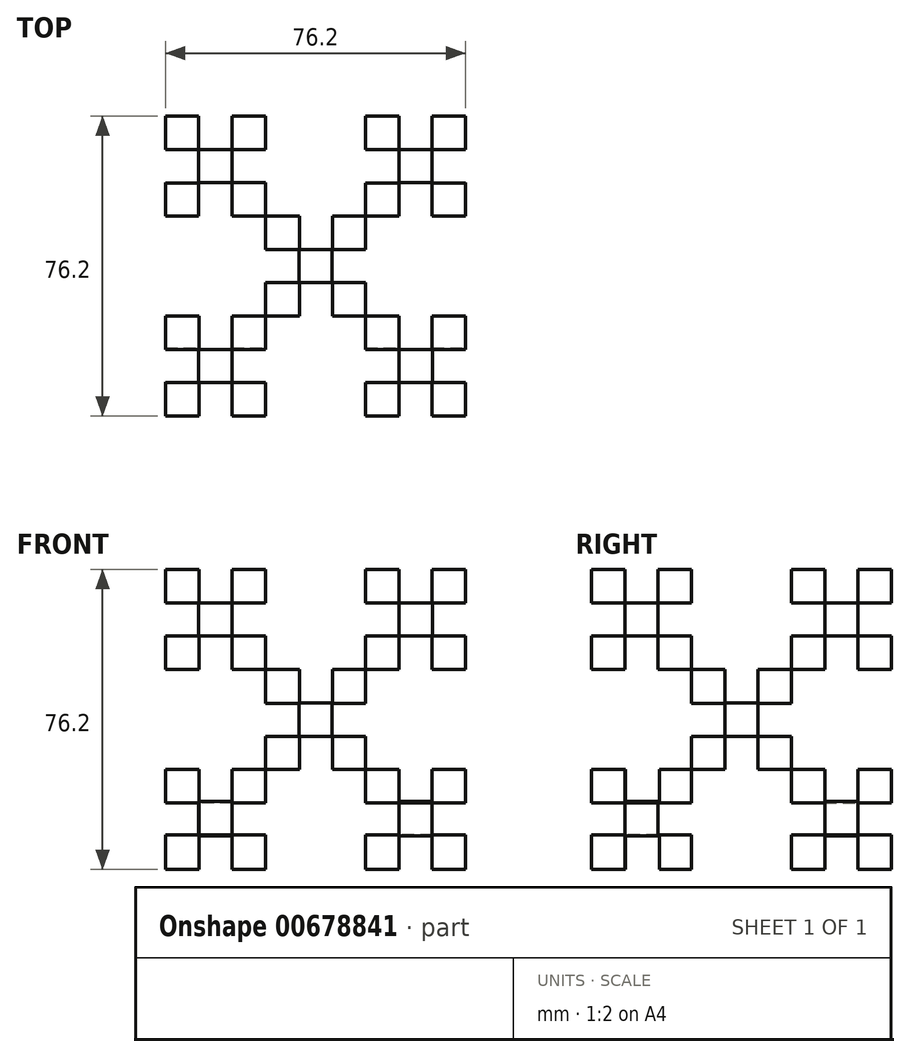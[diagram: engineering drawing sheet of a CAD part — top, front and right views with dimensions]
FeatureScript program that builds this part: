
annotation { "Feature Type Name" : "Feature", "Feature Type Description" : "" }
export const myFeature = defineFeature(function(context is Context, id is Id, definition is map)
    precondition{}
    {
        {
            var Q0;
            Q0=qCreatedBy(makeId("Front.planeOp"),FACE);
            var sketch = newSketch(context, id + "F0", { "sketchPlane" : qUnion([Q0])});
            skLineSegment(sketch, "E0.bottom", {"start": v(-38.1, 38.1) * mm, "end": v(38.1, 38.1) * mm});
            skLineSegment(sketch, "E0.top", {"start": v(-38.1, -38.1) * mm, "end": v(38.1, -38.1) * mm});
            skLineSegment(sketch, "E0.left", {"start": v(-38.1, 38.1) * mm, "end": v(-38.1, -38.1) * mm});
            skLineSegment(sketch, "E0.right", {"start": v(38.1, 38.1) * mm, "end": v(38.1, -38.1) * mm});
            skPoint(sketch, "E0.middle", {"position": v(0, 0) * mm});
            skSolve(sketch);
        }
        {
            var Q0;
            Q0=makeQuery(id+"F0.imprint","IMPRINT",FACE,{"disambiguationData":[TD([[makeQuery(id+"F0.imprint","IMPRINT",EDGE,{"derivedFrom":sQuery(id+"F0.wireOp",EDGE,"E0.bottom")}),-1.0]])]});
            extrude(context, id + "F1", {"entities" : qUnion([Q0]), "depth" : 76.2 * mm, "offsetDistance" : 25.4 * mm});
        }
        {
            var Q0;
            Q0=qCreatedBy(makeId("Front.planeOp"),FACE);
            var sketch = newSketch(context, id + "F2", { "sketchPlane" : qUnion([Q0])});
            skLineSegment(sketch, "E1.bottom", {"start": v(12.7, 12.7) * mm, "end": v(-12.7, 12.7) * mm});
            skLineSegment(sketch, "E1.top", {"start": v(12.7, -12.7) * mm, "end": v(-12.7, -12.7) * mm});
            skLineSegment(sketch, "E1.left", {"start": v(12.7, 12.7) * mm, "end": v(12.7, -12.7) * mm});
            skLineSegment(sketch, "E1.right", {"start": v(-12.7, 12.7) * mm, "end": v(-12.7, -12.7) * mm});
            skPoint(sketch, "E1.middle", {"position": v(0, 0) * mm});
            skLineSegment(sketch, "E2.top", {"start": v(12.7, 38.1) * mm, "end": v(-12.7, 38.1) * mm});
            skLineSegment(sketch, "E2.left", {"start": v(12.7, 12.7) * mm, "end": v(12.7, 38.1) * mm});
            skLineSegment(sketch, "E2.right", {"start": v(-12.7, 12.7) * mm, "end": v(-12.7, 38.1) * mm});
            skLineSegment(sketch, "E3.bottom", {"start": v(-12.7, 12.7) * mm, "end": v(-38.1, 12.7) * mm});
            skLineSegment(sketch, "E3.top", {"start": v(-12.7, -12.7) * mm, "end": v(-38.1, -12.7) * mm});
            skLineSegment(sketch, "E3.right", {"start": v(-38.1, 12.7) * mm, "end": v(-38.1, -12.7) * mm});
            skLineSegment(sketch, "E4.top", {"start": v(12.7, -38.1) * mm, "end": v(-12.7, -38.1) * mm});
            skLineSegment(sketch, "E4.left", {"start": v(12.7, -12.7) * mm, "end": v(12.7, -38.1) * mm});
            skLineSegment(sketch, "E4.right", {"start": v(-12.7, -12.7) * mm, "end": v(-12.7, -38.1) * mm});
            skLineSegment(sketch, "E5.bottom", {"start": v(12.7, 12.7) * mm, "end": v(38.1, 12.7) * mm});
            skLineSegment(sketch, "E5.top", {"start": v(12.7, -12.7) * mm, "end": v(38.1, -12.7) * mm});
            skLineSegment(sketch, "E5.right", {"start": v(38.1, 12.7) * mm, "end": v(38.1, -12.7) * mm});
            skSolve(sketch);
        }
        {
            var Q0;
            Q0 = qSketchRegion(id + "F2", true);
            extrude(context, id + "F3", {"entities" : qUnion([Q0]), "operationType" : NewBodyOperationType.REMOVE, "depth" : 25.4 * mm, "offsetDistance" : 25.4 * mm});
        }
        {
            var Q0;
            Q0=qCreatedBy(makeId("Front.planeOp"),FACE);
            cPlane(context, id + "F4", {"entities" : qUnion([Q0]), "cplaneType" : CPlaneType.OFFSET, "offset" : 76.2 * mm, "width" : 152.4 * mm, "height" : 152.4 * mm});
        }
        {
            var Q0;
            Q0=qCreatedBy(id+"F4.planeOp",FACE);
            var sketch = newSketch(context, id + "F5", { "sketchPlane" : qUnion([Q0])});
            skLineSegment(sketch, "E6.bottom", {"start": v(-12.7, 12.7) * mm, "end": v(12.7, 12.7) * mm});
            skLineSegment(sketch, "E6.top", {"start": v(-12.7, -12.7) * mm, "end": v(12.7, -12.7) * mm});
            skLineSegment(sketch, "E6.left", {"start": v(-12.7, 12.7) * mm, "end": v(-12.7, -12.7) * mm});
            skLineSegment(sketch, "E6.right", {"start": v(12.7, 12.7) * mm, "end": v(12.7, -12.7) * mm});
            skPoint(sketch, "E6.middle", {"position": v(0, 0) * mm});
            skLineSegment(sketch, "E7.top", {"start": v(-12.7, 38.1) * mm, "end": v(12.7, 38.1) * mm});
            skLineSegment(sketch, "E7.left", {"start": v(-12.7, 12.7) * mm, "end": v(-12.7, 38.1) * mm});
            skLineSegment(sketch, "E7.right", {"start": v(12.7, 12.7) * mm, "end": v(12.7, 38.1) * mm});
            skLineSegment(sketch, "E8.left", {"start": v(-12.7, -12.7) * mm, "end": v(-12.7, -12.7) * mm});
            skLineSegment(sketch, "E8.right", {"start": v(12.7, -12.7) * mm, "end": v(12.7, -12.7) * mm});
            skLineSegment(sketch, "E9.top", {"start": v(-12.7, -38.1) * mm, "end": v(12.7, -38.1) * mm});
            skLineSegment(sketch, "E9.left", {"start": v(-12.7, -12.7) * mm, "end": v(-12.7, -38.1) * mm});
            skLineSegment(sketch, "E9.right", {"start": v(12.7, -12.7) * mm, "end": v(12.7, -38.1) * mm});
            skLineSegment(sketch, "E10.bottom", {"start": v(12.7, 12.7) * mm, "end": v(38.1, 12.7) * mm});
            skLineSegment(sketch, "E10.top", {"start": v(12.7, -12.7) * mm, "end": v(38.1, -12.7) * mm});
            skLineSegment(sketch, "E10.right", {"start": v(38.1, 12.7) * mm, "end": v(38.1, -12.7) * mm});
            skLineSegment(sketch, "E11.bottom", {"start": v(-12.7, -12.7) * mm, "end": v(-38.1, -12.7) * mm});
            skLineSegment(sketch, "E11.top", {"start": v(-12.7, 12.7) * mm, "end": v(-38.1, 12.7) * mm});
            skLineSegment(sketch, "E11.left", {"start": v(-12.7, -12.7) * mm, "end": v(-12.7, 12.7) * mm});
            skLineSegment(sketch, "E11.right", {"start": v(-38.1, -12.7) * mm, "end": v(-38.1, 12.7) * mm});
            skSolve(sketch);
        }
        {
            var Q0;
            Q0 = qSketchRegion(id + "F5", true);
            extrude(context, id + "F6", {"entities" : qUnion([Q0]), "operationType" : NewBodyOperationType.REMOVE, "oppositeDirection" : true, "depth" : 25.4 * mm, "offsetDistance" : 25.4 * mm});
        }
        {
            var Q0;
            Q0=qCreatedBy(makeId("Top.planeOp"),FACE);
            cPlane(context, id + "F7", {"entities" : qUnion([Q0]), "cplaneType" : CPlaneType.OFFSET, "offset" : 38.1 * mm, "width" : 152.4 * mm, "height" : 152.4 * mm});
        }
        {
            var Q0;
            Q0=qCreatedBy(id+"F7.planeOp",FACE);
            var sketch = newSketch(context, id + "F8", { "sketchPlane" : qUnion([Q0])});
            skLineSegment(sketch, "E12.bottom", {"start": v(-12.7, -25.4) * mm, "end": v(12.7, -25.4) * mm});
            skLineSegment(sketch, "E12.top", {"start": v(-12.7, -50.8) * mm, "end": v(12.7, -50.8) * mm});
            skLineSegment(sketch, "E12.left", {"start": v(-12.7, -25.4) * mm, "end": v(-12.7, -50.8) * mm});
            skLineSegment(sketch, "E12.right", {"start": v(12.7, -25.4) * mm, "end": v(12.7, -50.8) * mm});
            skPoint(sketch, "E12.middle", {"position": v(0, -38.1) * mm});
            skLineSegment(sketch, "E13.bottom", {"start": v(12.7, -25.4) * mm, "end": v(38.1, -25.4) * mm});
            skLineSegment(sketch, "E13.top", {"start": v(12.7, -50.8) * mm, "end": v(38.1, -50.8) * mm});
            skLineSegment(sketch, "E13.right", {"start": v(38.1, -25.4) * mm, "end": v(38.1, -50.8) * mm});
            skLineSegment(sketch, "E14.bottom", {"start": v(-12.7, -25.4) * mm, "end": v(-38.1, -25.4) * mm});
            skLineSegment(sketch, "E14.top", {"start": v(-12.7, -50.8) * mm, "end": v(-38.1, -50.8) * mm});
            skLineSegment(sketch, "E14.right", {"start": v(-38.1, -25.4) * mm, "end": v(-38.1, -50.8) * mm});
            skSolve(sketch);
        }
        {
            var Q0;
            Q0 = qSketchRegion(id + "F8", true);
            extrude(context, id + "F9", {"entities" : qUnion([Q0]), "operationType" : NewBodyOperationType.REMOVE, "oppositeDirection" : true, "depth" : 25.4 * mm, "offsetDistance" : 25.4 * mm});
        }
        {
            var Q0;
            Q0=qCreatedBy(makeId("Right.planeOp"),FACE);
            cPlane(context, id + "F10", {"entities" : qUnion([Q0]), "cplaneType" : CPlaneType.OFFSET, "offset" : 38.1 * mm, "width" : 152.4 * mm, "height" : 152.4 * mm});
        }
        {
            var Q0;
            Q0=qCreatedBy(id+"F10.planeOp",FACE);
            var sketch = newSketch(context, id + "F11", { "sketchPlane" : qUnion([Q0])});
            skLineSegment(sketch, "E15", {"start": v(0, 0) * mm, "end": v(-38.1, 0) * mm});
            skLineSegment(sketch, "E16.bottom", {"start": v(-50.8, 12.7) * mm, "end": v(-25.4, 12.7) * mm});
            skLineSegment(sketch, "E16.top", {"start": v(-50.8, -12.7) * mm, "end": v(-25.4, -12.7) * mm});
            skLineSegment(sketch, "E16.left", {"start": v(-50.8, 12.7) * mm, "end": v(-50.8, -12.7) * mm});
            skLineSegment(sketch, "E16.right", {"start": v(-25.4, 12.7) * mm, "end": v(-25.4, -12.7) * mm});
            skPoint(sketch, "E16.middle", {"position": v(-38.1, 0) * mm});
            skLineSegment(sketch, "E17.bottom", {"start": v(-25.4, -12.7) * mm, "end": v(-50.8, -12.7) * mm});
            skLineSegment(sketch, "E17.top", {"start": v(-25.4, -38.1) * mm, "end": v(-50.8, -38.1) * mm});
            skLineSegment(sketch, "E17.left", {"start": v(-25.4, -12.7) * mm, "end": v(-25.4, -38.1) * mm});
            skLineSegment(sketch, "E17.right", {"start": v(-50.8, -12.7) * mm, "end": v(-50.8, -38.1) * mm});
            skSolve(sketch);
        }
        {
            var Q0;
            Q0 = qSketchRegion(id + "F11", true);
            extrude(context, id + "F12", {"entities" : qUnion([Q0]), "operationType" : NewBodyOperationType.REMOVE, "oppositeDirection" : true, "depth" : 25.4 * mm, "offsetDistance" : 25.4 * mm});
        }
        {
            var Q0;
            Q0=qCreatedBy(makeId("Top.planeOp"),FACE);
            cPlane(context, id + "F13", {"entities" : qUnion([Q0]), "cplaneType" : CPlaneType.OFFSET, "offset" : 38.1 * mm, "oppositeDirection" : true, "width" : 152.4 * mm, "height" : 152.4 * mm});
        }
        {
            var Q0;
            Q0=qCreatedBy(id+"F13.planeOp",FACE);
            var sketch = newSketch(context, id + "F14", { "sketchPlane" : qUnion([Q0])});
            skLineSegment(sketch, "E18", {"start": v(0, 0) * mm, "end": v(0, -38.1) * mm});
            skLineSegment(sketch, "E19.bottom", {"start": v(-12.7, -50.8) * mm, "end": v(12.7, -50.8) * mm});
            skLineSegment(sketch, "E19.top", {"start": v(-12.7, -25.4) * mm, "end": v(12.7, -25.4) * mm});
            skLineSegment(sketch, "E19.left", {"start": v(-12.7, -50.8) * mm, "end": v(-12.7, -25.4) * mm});
            skLineSegment(sketch, "E19.right", {"start": v(12.7, -50.8) * mm, "end": v(12.7, -25.4) * mm});
            skPoint(sketch, "E19.middle", {"position": v(0, -38.1) * mm});
            skLineSegment(sketch, "E20.bottom", {"start": v(-12.7, -50.8) * mm, "end": v(-38.1, -50.8) * mm});
            skLineSegment(sketch, "E20.top", {"start": v(-12.7, -25.4) * mm, "end": v(-38.1, -25.4) * mm});
            skLineSegment(sketch, "E20.right", {"start": v(-38.1, -50.8) * mm, "end": v(-38.1, -25.4) * mm});
            skSolve(sketch);
        }
        {
            var Q0;
            Q0 = qSketchRegion(id + "F14", true);
            extrude(context, id + "F15", {"entities" : qUnion([Q0]), "operationType" : NewBodyOperationType.REMOVE, "depth" : 25.4 * mm, "offsetDistance" : 25.4 * mm});
        }
        {
            var Q0;
            Q0=qCreatedBy(makeId("Right.planeOp"),FACE);
            cPlane(context, id + "F16", {"entities" : qUnion([Q0]), "cplaneType" : CPlaneType.OFFSET, "offset" : 38.1 * mm, "oppositeDirection" : true, "width" : 152.4 * mm, "height" : 152.4 * mm});
        }
        {
            var Q0;
            Q0=qCreatedBy(id+"F16.planeOp",FACE);
            var sketch = newSketch(context, id + "F17", { "sketchPlane" : qUnion([Q0])});
            skLineSegment(sketch, "E21.bottom", {"start": v(-25.4, 12.7) * mm, "end": v(-50.8, 12.7) * mm});
            skLineSegment(sketch, "E21.top", {"start": v(-25.4, -12.7) * mm, "end": v(-50.8, -12.7) * mm});
            skLineSegment(sketch, "E21.left", {"start": v(-25.4, 12.7) * mm, "end": v(-25.4, -12.7) * mm});
            skLineSegment(sketch, "E21.right", {"start": v(-50.8, 12.7) * mm, "end": v(-50.8, -12.7) * mm});
            skPoint(sketch, "E21.middle", {"position": v(-38.1, 0) * mm});
            skSolve(sketch);
        }
        {
            var Q0;
            Q0 = qSketchRegion(id + "F17", true);
            extrude(context, id + "F18", {"entities" : qUnion([Q0]), "operationType" : NewBodyOperationType.REMOVE, "depth" : 25.4 * mm, "offsetDistance" : 25.4 * mm});
        }
        {
            var Q0;
            Q0=qCreatedBy(id+"F10.planeOp",FACE);
            var sketch = newSketch(context, id + "F19", { "sketchPlane" : qUnion([Q0])});
            skLineSegment(sketch, "E22.bottom", {"start": v(-8.48, 29.64) * mm, "end": v(-16.95, 29.64) * mm});
            skLineSegment(sketch, "E22.top", {"start": v(-8.48, 21.18) * mm, "end": v(-16.95, 21.18) * mm});
            skLineSegment(sketch, "E22.left", {"start": v(-8.48, 29.64) * mm, "end": v(-8.48, 21.18) * mm});
            skLineSegment(sketch, "E22.right", {"start": v(-16.95, 29.64) * mm, "end": v(-16.95, 21.18) * mm});
            skPoint(sketch, "E22.middle", {"position": v(-12.72, 25.41) * mm});
            skLineSegment(sketch, "E23.top", {"start": v(-8.48, 38.1) * mm, "end": v(-16.95, 38.1) * mm});
            skLineSegment(sketch, "E23.left", {"start": v(-8.48, 29.64) * mm, "end": v(-8.48, 38.1) * mm});
            skLineSegment(sketch, "E23.right", {"start": v(-16.95, 29.64) * mm, "end": v(-16.95, 38.1) * mm});
            skLineSegment(sketch, "E24.top", {"start": v(-8.48, 12.7) * mm, "end": v(-16.95, 12.7) * mm});
            skLineSegment(sketch, "E24.left", {"start": v(-8.48, 38.1) * mm, "end": v(-8.48, 12.7) * mm});
            skLineSegment(sketch, "E24.right", {"start": v(-16.95, 38.1) * mm, "end": v(-16.95, 12.7) * mm});
            skLineSegment(sketch, "E25.bottom", {"start": v(0, 21.19) * mm, "end": v(0, 29.64) * mm});
            skLineSegment(sketch, "E25.top", {"start": v(-25.4, 21.19) * mm, "end": v(-25.4, 29.64) * mm});
            skLineSegment(sketch, "E25.left", {"start": v(0, 21.19) * mm, "end": v(-25.4, 21.19) * mm});
            skLineSegment(sketch, "E25.right", {"start": v(0, 29.64) * mm, "end": v(-25.4, 29.64) * mm});
            skLineSegment(sketch, "E26.bottom", {"start": v(-8.48, -21.17) * mm, "end": v(-16.95, -21.17) * mm});
            skLineSegment(sketch, "E26.top", {"start": v(-8.48, -29.62) * mm, "end": v(-16.95, -29.62) * mm});
            skLineSegment(sketch, "E26.left", {"start": v(-8.48, -21.17) * mm, "end": v(-8.48, -29.62) * mm});
            skLineSegment(sketch, "E26.right", {"start": v(-16.95, -21.17) * mm, "end": v(-16.95, -29.62) * mm});
            skPoint(sketch, "E26.middle", {"position": v(-12.72, -25.4) * mm});
            skLineSegment(sketch, "E27.top", {"start": v(-8.48, -12.7) * mm, "end": v(-16.95, -12.7) * mm});
            skLineSegment(sketch, "E27.left", {"start": v(-8.48, -21.17) * mm, "end": v(-8.48, -12.7) * mm});
            skLineSegment(sketch, "E27.right", {"start": v(-16.95, -21.17) * mm, "end": v(-16.95, -12.7) * mm});
            skLineSegment(sketch, "E28.top", {"start": v(-8.48, -38.1) * mm, "end": v(-16.95, -38.1) * mm});
            skLineSegment(sketch, "E28.left", {"start": v(-8.48, -12.7) * mm, "end": v(-8.48, -38.1) * mm});
            skLineSegment(sketch, "E28.right", {"start": v(-16.95, -12.7) * mm, "end": v(-16.95, -38.1) * mm});
            skLineSegment(sketch, "E29.bottom", {"start": v(0, -29.32) * mm, "end": v(0, -21.17) * mm});
            skLineSegment(sketch, "E29.top", {"start": v(-25.4, -29.32) * mm, "end": v(-25.4, -21.17) * mm});
            skLineSegment(sketch, "E29.left", {"start": v(0, -29.32) * mm, "end": v(-25.4, -29.32) * mm});
            skLineSegment(sketch, "E29.right", {"start": v(0, -21.17) * mm, "end": v(-25.4, -21.17) * mm});
            skLineSegment(sketch, "E30.bottom", {"start": v(-58.95, -21.17) * mm, "end": v(-67.42, -21.17) * mm});
            skLineSegment(sketch, "E30.top", {"start": v(-58.95, -29.62) * mm, "end": v(-67.42, -29.62) * mm});
            skLineSegment(sketch, "E30.left", {"start": v(-58.95, -21.17) * mm, "end": v(-58.95, -29.62) * mm});
            skLineSegment(sketch, "E30.right", {"start": v(-67.42, -21.17) * mm, "end": v(-67.42, -29.62) * mm});
            skPoint(sketch, "E30.middle", {"position": v(-63.18, -25.4) * mm});
            skLineSegment(sketch, "E31.top", {"start": v(-58.95, -12.7) * mm, "end": v(-67.42, -12.7) * mm});
            skLineSegment(sketch, "E31.left", {"start": v(-58.95, -21.17) * mm, "end": v(-58.95, -12.7) * mm});
            skLineSegment(sketch, "E31.right", {"start": v(-67.42, -21.17) * mm, "end": v(-67.42, -12.7) * mm});
            skLineSegment(sketch, "E32.top", {"start": v(-58.95, -38.1) * mm, "end": v(-67.42, -38.1) * mm});
            skLineSegment(sketch, "E32.left", {"start": v(-58.95, -12.7) * mm, "end": v(-58.95, -38.1) * mm});
            skLineSegment(sketch, "E32.right", {"start": v(-67.42, -12.7) * mm, "end": v(-67.42, -38.1) * mm});
            skLineSegment(sketch, "E33.bottom", {"start": v(-50.8, -29.32) * mm, "end": v(-50.8, -21.17) * mm});
            skLineSegment(sketch, "E33.top", {"start": v(-76.2, -29.32) * mm, "end": v(-76.2, -21.17) * mm});
            skLineSegment(sketch, "E33.left", {"start": v(-50.8, -29.32) * mm, "end": v(-76.2, -29.32) * mm});
            skLineSegment(sketch, "E33.right", {"start": v(-50.8, -21.17) * mm, "end": v(-76.2, -21.17) * mm});
            skLineSegment(sketch, "E34.left", {"start": v(-8.48, 21.18) * mm, "end": v(-8.48, 29.64) * mm});
            skLineSegment(sketch, "E34.right", {"start": v(-16.95, 21.18) * mm, "end": v(-16.95, 29.64) * mm});
            skLineSegment(sketch, "E35.bottom", {"start": v(-58.95, -21.17) * mm, "end": v(-67.42, -21.16) * mm});
            skLineSegment(sketch, "E35.right", {"start": v(-67.42, -21.16) * mm, "end": v(-67.42, -29.62) * mm});
            skLineSegment(sketch, "E36.bottom", {"start": v(-67.74, 38.1) * mm, "end": v(-59.28, 38.1) * mm});
            skLineSegment(sketch, "E36.top", {"start": v(-67.74, 12.7) * mm, "end": v(-59.28, 12.7) * mm});
            skLineSegment(sketch, "E36.left", {"start": v(-67.74, 38.1) * mm, "end": v(-67.74, 12.7) * mm});
            skLineSegment(sketch, "E36.right", {"start": v(-59.28, 38.1) * mm, "end": v(-59.28, 12.7) * mm});
            skLineSegment(sketch, "E37.bottom", {"start": v(-76.2, 29.64) * mm, "end": v(-50.8, 29.64) * mm});
            skLineSegment(sketch, "E37.top", {"start": v(-76.2, 21.18) * mm, "end": v(-50.8, 21.18) * mm});
            skLineSegment(sketch, "E37.left", {"start": v(-76.2, 29.64) * mm, "end": v(-76.2, 21.18) * mm});
            skLineSegment(sketch, "E37.right", {"start": v(-50.8, 29.64) * mm, "end": v(-50.8, 21.18) * mm});
            skSolve(sketch);
        }
        {
            var Q0;
            Q0 = qSketchRegion(id + "F19", true);
            extrude(context, id + "F20", {"entities" : qUnion([Q0]), "operationType" : NewBodyOperationType.REMOVE, "oppositeDirection" : true, "depth" : 131.57 * mm, "offsetDistance" : 25.4 * mm});
        }
        {
            var Q0;
            Q0=qCreatedBy(id+"F16.planeOp",FACE);
            var sketch = newSketch(context, id + "F21", { "sketchPlane" : qUnion([Q0])});
            skLineSegment(sketch, "E38.bottom", {"start": v(-8.46, 29.64) * mm, "end": v(-16.93, 29.64) * mm});
            skLineSegment(sketch, "E38.top", {"start": v(-8.46, 21.18) * mm, "end": v(-16.93, 21.18) * mm});
            skLineSegment(sketch, "E38.left", {"start": v(-8.46, 29.64) * mm, "end": v(-8.46, 21.18) * mm});
            skLineSegment(sketch, "E38.right", {"start": v(-16.93, 29.64) * mm, "end": v(-16.93, 21.18) * mm});
            skPoint(sketch, "E38.middle", {"position": v(-12.7, 25.41) * mm});
            skLineSegment(sketch, "E39.top", {"start": v(-8.46, 38.1) * mm, "end": v(-16.93, 38.1) * mm});
            skLineSegment(sketch, "E39.left", {"start": v(-8.46, 29.64) * mm, "end": v(-8.46, 38.1) * mm});
            skLineSegment(sketch, "E39.right", {"start": v(-16.93, 29.64) * mm, "end": v(-16.93, 38.1) * mm});
            skLineSegment(sketch, "E40.top", {"start": v(-8.46, 12.7) * mm, "end": v(-16.93, 12.7) * mm});
            skLineSegment(sketch, "E40.left", {"start": v(-8.46, 38.1) * mm, "end": v(-8.46, 12.7) * mm});
            skLineSegment(sketch, "E40.right", {"start": v(-16.93, 38.1) * mm, "end": v(-16.93, 12.7) * mm});
            skLineSegment(sketch, "E41.bottom", {"start": v(0, 21.16) * mm, "end": v(0, 29.64) * mm});
            skLineSegment(sketch, "E41.top", {"start": v(-25.4, 21.16) * mm, "end": v(-25.4, 29.64) * mm});
            skLineSegment(sketch, "E41.left", {"start": v(0, 21.16) * mm, "end": v(-25.4, 21.16) * mm});
            skLineSegment(sketch, "E41.right", {"start": v(0, 29.64) * mm, "end": v(-25.4, 29.64) * mm});
            skLineSegment(sketch, "E42.bottom", {"start": v(-59.26, 29.64) * mm, "end": v(-67.73, 29.64) * mm});
            skLineSegment(sketch, "E42.top", {"start": v(-59.26, 21.18) * mm, "end": v(-67.73, 21.18) * mm});
            skLineSegment(sketch, "E42.left", {"start": v(-59.26, 29.64) * mm, "end": v(-59.26, 21.18) * mm});
            skLineSegment(sketch, "E42.right", {"start": v(-67.73, 29.64) * mm, "end": v(-67.73, 21.18) * mm});
            skPoint(sketch, "E42.middle", {"position": v(-63.5, 25.41) * mm});
            skLineSegment(sketch, "E43.top", {"start": v(-59.26, 38.1) * mm, "end": v(-67.73, 38.1) * mm});
            skLineSegment(sketch, "E43.left", {"start": v(-59.26, 29.64) * mm, "end": v(-59.26, 38.1) * mm});
            skLineSegment(sketch, "E43.right", {"start": v(-67.73, 29.64) * mm, "end": v(-67.73, 38.1) * mm});
            skLineSegment(sketch, "E44.top", {"start": v(-59.26, 12.7) * mm, "end": v(-67.73, 12.7) * mm});
            skLineSegment(sketch, "E44.left", {"start": v(-59.26, 38.1) * mm, "end": v(-59.26, 12.7) * mm});
            skLineSegment(sketch, "E44.right", {"start": v(-67.73, 38.1) * mm, "end": v(-67.73, 12.7) * mm});
            skLineSegment(sketch, "E45.bottom", {"start": v(-50.8, 21.16) * mm, "end": v(-50.8, 29.64) * mm});
            skLineSegment(sketch, "E45.top", {"start": v(-76.2, 21.16) * mm, "end": v(-76.2, 29.64) * mm});
            skLineSegment(sketch, "E45.left", {"start": v(-50.8, 21.16) * mm, "end": v(-76.2, 21.16) * mm});
            skLineSegment(sketch, "E45.right", {"start": v(-50.8, 29.64) * mm, "end": v(-76.2, 29.64) * mm});
            skLineSegment(sketch, "E46.bottom", {"start": v(-8.46, -21.16) * mm, "end": v(-16.93, -21.16) * mm});
            skLineSegment(sketch, "E46.left", {"start": v(-8.46, -21.16) * mm, "end": v(-8.46, -29.62) * mm});
            skLineSegment(sketch, "E46.right", {"start": v(-16.93, -21.16) * mm, "end": v(-16.93, -29.62) * mm});
            skPoint(sketch, "E46.middle", {"position": v(-12.7, -25.39) * mm});
            skLineSegment(sketch, "E47.top", {"start": v(-8.46, -12.7) * mm, "end": v(-16.93, -12.7) * mm});
            skLineSegment(sketch, "E47.left", {"start": v(-8.46, -21.16) * mm, "end": v(-8.46, -12.7) * mm});
            skLineSegment(sketch, "E47.right", {"start": v(-16.93, -21.16) * mm, "end": v(-16.93, -12.7) * mm});
            skLineSegment(sketch, "E48.top", {"start": v(-8.46, -38.1) * mm, "end": v(-16.93, -38.1) * mm});
            skLineSegment(sketch, "E48.left", {"start": v(-8.46, -12.7) * mm, "end": v(-8.46, -38.1) * mm});
            skLineSegment(sketch, "E48.right", {"start": v(-16.93, -12.7) * mm, "end": v(-16.93, -38.1) * mm});
            skLineSegment(sketch, "E49.bottom", {"start": v(0, -29.34) * mm, "end": v(0, -21.16) * mm});
            skLineSegment(sketch, "E49.top", {"start": v(-25.4, -29.34) * mm, "end": v(-25.4, -21.16) * mm});
            skLineSegment(sketch, "E49.left", {"start": v(0, -29.34) * mm, "end": v(-25.4, -29.34) * mm});
            skLineSegment(sketch, "E49.right", {"start": v(0, -21.16) * mm, "end": v(-25.4, -21.16) * mm});
            skLineSegment(sketch, "E50.bottom", {"start": v(-59.05, -21.16) * mm, "end": v(-67.52, -21.16) * mm});
            skLineSegment(sketch, "E50.top", {"start": v(-59.05, -29.62) * mm, "end": v(-67.52, -29.62) * mm});
            skLineSegment(sketch, "E50.left", {"start": v(-59.05, -21.16) * mm, "end": v(-59.05, -29.62) * mm});
            skLineSegment(sketch, "E50.right", {"start": v(-67.52, -21.16) * mm, "end": v(-67.52, -29.62) * mm});
            skPoint(sketch, "E50.middle", {"position": v(-63.29, -25.39) * mm});
            skLineSegment(sketch, "E51.top", {"start": v(-59.05, -12.7) * mm, "end": v(-67.52, -12.7) * mm});
            skLineSegment(sketch, "E51.left", {"start": v(-59.05, -21.16) * mm, "end": v(-59.05, -12.7) * mm});
            skLineSegment(sketch, "E51.right", {"start": v(-67.52, -21.16) * mm, "end": v(-67.52, -12.7) * mm});
            skLineSegment(sketch, "E52.top", {"start": v(-59.05, -38.1) * mm, "end": v(-67.52, -38.1) * mm});
            skLineSegment(sketch, "E52.left", {"start": v(-59.05, -12.7) * mm, "end": v(-59.05, -38.1) * mm});
            skLineSegment(sketch, "E52.right", {"start": v(-67.52, -12.7) * mm, "end": v(-67.52, -38.1) * mm});
            skLineSegment(sketch, "E53.bottom", {"start": v(-50.8, -29.34) * mm, "end": v(-50.8, -21.16) * mm});
            skLineSegment(sketch, "E53.top", {"start": v(-76.2, -29.34) * mm, "end": v(-76.2, -21.16) * mm});
            skLineSegment(sketch, "E53.left", {"start": v(-50.8, -29.34) * mm, "end": v(-76.2, -29.34) * mm});
            skLineSegment(sketch, "E53.right", {"start": v(-50.8, -21.16) * mm, "end": v(-76.2, -21.16) * mm});
            skLineSegment(sketch, "E54.left", {"start": v(-8.46, 21.18) * mm, "end": v(-8.46, 29.64) * mm});
            skLineSegment(sketch, "E54.right", {"start": v(-16.93, 21.18) * mm, "end": v(-16.93, 29.64) * mm});
            skLineSegment(sketch, "E55.bottom", {"start": v(-8.46, -21.16) * mm, "end": v(-17.05, -21.2) * mm});
            skLineSegment(sketch, "E55.left", {"start": v(-8.46, -21.16) * mm, "end": v(-8.33, -29.65) * mm});
            skLineSegment(sketch, "E55.right", {"start": v(-17.05, -21.2) * mm, "end": v(-16.93, -29.62) * mm});
            skLineSegment(sketch, "E56.bottom", {"start": v(-59.05, -21.16) * mm, "end": v(-67.52, -21.19) * mm});
            skLineSegment(sketch, "E56.left", {"start": v(-59.05, -21.16) * mm, "end": v(-59.05, -29.65) * mm});
            skLineSegment(sketch, "E56.right", {"start": v(-67.52, -21.19) * mm, "end": v(-67.52, -29.62) * mm});
            skSolve(sketch);
        }
        {
            var Q0;
            Q0 = qSketchRegion(id + "F21", true);
            extrude(context, id + "F22", {"entities" : qUnion([Q0]), "operationType" : NewBodyOperationType.REMOVE, "depth" : 8.46 * mm, "offsetDistance" : 25.4 * mm});
        }
        {
            var Q0;
            Q0=qCreatedBy(id+"F7.planeOp",FACE);
            var sketch = newSketch(context, id + "F23", { "sketchPlane" : qUnion([Q0])});
            skLineSegment(sketch, "E57.bottom", {"start": v(21.17, 0) * mm, "end": v(29.62, 0) * mm});
            skLineSegment(sketch, "E57.top", {"start": v(21.17, -25.4) * mm, "end": v(29.62, -25.4) * mm});
            skLineSegment(sketch, "E57.left", {"start": v(21.17, 0) * mm, "end": v(21.17, -25.4) * mm});
            skLineSegment(sketch, "E57.right", {"start": v(29.62, 0) * mm, "end": v(29.62, -25.4) * mm});
            skLineSegment(sketch, "E58.bottom", {"start": v(12.66, -16.98) * mm, "end": v(12.66, -8.52) * mm});
            skLineSegment(sketch, "E58.top", {"start": v(38.06, -16.98) * mm, "end": v(38.06, -8.52) * mm});
            skLineSegment(sketch, "E58.left", {"start": v(12.66, -16.98) * mm, "end": v(38.06, -16.98) * mm});
            skLineSegment(sketch, "E58.right", {"start": v(12.66, -8.52) * mm, "end": v(38.06, -8.52) * mm});
            skLineSegment(sketch, "E59.bottom", {"start": v(-29.69, 0) * mm, "end": v(-21.23, 0) * mm});
            skLineSegment(sketch, "E59.top", {"start": v(-29.69, -25.4) * mm, "end": v(-21.23, -25.4) * mm});
            skLineSegment(sketch, "E59.left", {"start": v(-29.69, 0) * mm, "end": v(-29.69, -25.4) * mm});
            skLineSegment(sketch, "E59.right", {"start": v(-21.23, 0) * mm, "end": v(-21.23, -25.4) * mm});
            skLineSegment(sketch, "E60.bottom", {"start": v(-12.7, -8.47) * mm, "end": v(-12.68, -16.93) * mm});
            skLineSegment(sketch, "E60.top", {"start": v(-38.1, -8.52) * mm, "end": v(-38.08, -16.98) * mm});
            skLineSegment(sketch, "E60.left", {"start": v(-12.7, -8.47) * mm, "end": v(-38.1, -8.52) * mm});
            skLineSegment(sketch, "E60.right", {"start": v(-12.68, -16.93) * mm, "end": v(-38.08, -16.98) * mm});
            skLineSegment(sketch, "E61.bottom", {"start": v(-29.66, -50.8) * mm, "end": v(-21.2, -50.8) * mm});
            skLineSegment(sketch, "E61.top", {"start": v(-29.66, -76.2) * mm, "end": v(-21.2, -76.2) * mm});
            skLineSegment(sketch, "E61.left", {"start": v(-29.66, -50.8) * mm, "end": v(-29.66, -76.2) * mm});
            skLineSegment(sketch, "E61.right", {"start": v(-21.2, -50.8) * mm, "end": v(-21.2, -76.2) * mm});
            skLineSegment(sketch, "E62", {"start": v(-12.68, -38.1) * mm, "end": v(-12.68, -59.27) * mm});
            skLineSegment(sketch, "E63.bottom", {"start": v(-12.68, -59.27) * mm, "end": v(-12.68, -67.73) * mm});
            skLineSegment(sketch, "E63.top", {"start": v(-38.08, -59.27) * mm, "end": v(-38.08, -67.73) * mm});
            skLineSegment(sketch, "E63.left", {"start": v(-12.68, -59.27) * mm, "end": v(-38.08, -59.27) * mm});
            skLineSegment(sketch, "E63.right", {"start": v(-12.68, -67.73) * mm, "end": v(-38.08, -67.73) * mm});
            skLineSegment(sketch, "E64.bottom", {"start": v(21.18, -50.8) * mm, "end": v(29.64, -50.8) * mm});
            skLineSegment(sketch, "E64.top", {"start": v(21.18, -76.2) * mm, "end": v(29.64, -76.2) * mm});
            skLineSegment(sketch, "E64.left", {"start": v(21.18, -50.8) * mm, "end": v(21.18, -76.2) * mm});
            skLineSegment(sketch, "E64.right", {"start": v(29.64, -50.8) * mm, "end": v(29.64, -76.2) * mm});
            skLineSegment(sketch, "E65.bottom", {"start": v(38.1, -59.28) * mm, "end": v(38.1, -67.74) * mm});
            skLineSegment(sketch, "E65.top", {"start": v(12.7, -59.28) * mm, "end": v(12.7, -67.74) * mm});
            skLineSegment(sketch, "E65.left", {"start": v(38.1, -59.28) * mm, "end": v(12.7, -59.28) * mm});
            skLineSegment(sketch, "E65.right", {"start": v(38.1, -67.74) * mm, "end": v(12.7, -67.74) * mm});
            skSolve(sketch);
        }
        {
            var Q0;
            Q0 = qSketchRegion(id + "F23", true);
            extrude(context, id + "F24", {"entities" : qUnion([Q0]), "operationType" : NewBodyOperationType.REMOVE, "oppositeDirection" : true, "depth" : 83.31 * mm, "offsetDistance" : 25.4 * mm});
        }
        {
            var Q0;
            Q0=qCreatedBy(id+"F10.planeOp",FACE);
            cPlane(context, id + "F25", {"entities" : qUnion([Q0]), "cplaneType" : CPlaneType.OFFSET, "offset" : 25.4 * mm, "oppositeDirection" : true, "width" : 152.4 * mm, "height" : 152.4 * mm});
        }
        {
            var Q0;
            Q0=qCreatedBy(id+"F25.planeOp",FACE);
            var sketch = newSketch(context, id + "F26", { "sketchPlane" : qUnion([Q0])});
            skLineSegment(sketch, "E66", {"start": v(-42.34, 0) * mm, "end": v(-42.34, 12.7) * mm});
            skLineSegment(sketch, "E67.bottom", {"start": v(-42.34, 12.7) * mm, "end": v(-33.88, 12.7) * mm});
            skLineSegment(sketch, "E67.top", {"start": v(-42.34, -12.7) * mm, "end": v(-33.88, -12.7) * mm});
            skLineSegment(sketch, "E67.left", {"start": v(-42.34, 12.7) * mm, "end": v(-42.34, -12.7) * mm});
            skLineSegment(sketch, "E67.right", {"start": v(-33.88, 12.7) * mm, "end": v(-33.88, -12.7) * mm});
            skLineSegment(sketch, "E68", {"start": v(-38.1, 4.11) * mm, "end": v(-25.4, 4.11) * mm});
            skLineSegment(sketch, "E69.bottom", {"start": v(-25.4, 4.11) * mm, "end": v(-25.4, -4.34) * mm});
            skLineSegment(sketch, "E69.top", {"start": v(-50.8, 4.11) * mm, "end": v(-50.8, -4.34) * mm});
            skLineSegment(sketch, "E69.left", {"start": v(-25.4, 4.11) * mm, "end": v(-50.8, 4.11) * mm});
            skLineSegment(sketch, "E69.right", {"start": v(-25.4, -4.34) * mm, "end": v(-50.8, -4.34) * mm});
            skSolve(sketch);
        }
        {
            var Q0;
            Q0 = qSketchRegion(id + "F26", true);
            extrude(context, id + "F27", {"entities" : qUnion([Q0]), "operationType" : NewBodyOperationType.REMOVE, "oppositeDirection" : true, "depth" : 25.4 * mm, "offsetDistance" : 25.4 * mm});
        }
        {
            var Q0;
            Q0=qCreatedBy(makeId("Front.planeOp"),FACE);
            cPlane(context, id + "F28", {"entities" : qUnion([Q0]), "cplaneType" : CPlaneType.OFFSET, "offset" : 25.4 * mm, "width" : 152.4 * mm, "height" : 152.4 * mm});
        }
        {
            var Q0;
            Q0=qCreatedBy(id+"F28.planeOp",FACE);
            var sketch = newSketch(context, id + "F29", { "sketchPlane" : qUnion([Q0])});
            skLineSegment(sketch, "E70", {"start": v(-4.12, 0) * mm, "end": v(-4.12, 12.7) * mm});
            skLineSegment(sketch, "E71.bottom", {"start": v(-4.12, 12.7) * mm, "end": v(4.33, 12.7) * mm});
            skLineSegment(sketch, "E71.top", {"start": v(-4.12, -12.7) * mm, "end": v(4.33, -12.7) * mm});
            skLineSegment(sketch, "E71.left", {"start": v(-4.12, 12.7) * mm, "end": v(-4.12, -12.7) * mm});
            skLineSegment(sketch, "E71.right", {"start": v(4.33, 12.7) * mm, "end": v(4.33, -12.7) * mm});
            skLineSegment(sketch, "E72", {"start": v(12.8, 12.72) * mm, "end": v(-12.64, 12.72) * mm});
            skSolve(sketch);
        }
        {
            var Q0;
            Q0 = qSketchRegion(id + "F29", true);
            extrude(context, id + "F30", {"entities" : qUnion([Q0]), "operationType" : NewBodyOperationType.REMOVE, "depth" : 47.5 * mm, "offsetDistance" : 25.4 * mm});
        }
        {
            var Q0;
            Q0=qCreatedBy(makeId("Front.planeOp"),FACE);
            cPlane(context, id + "F31", {"entities" : qUnion([Q0]), "cplaneType" : CPlaneType.OFFSET, "offset" : 8.46 * mm, "width" : 152.4 * mm, "height" : 152.4 * mm});
        }
        {
            var Q0;
            Q0=qCreatedBy(id+"F31.planeOp",FACE);
            var sketch = newSketch(context, id + "F32", { "sketchPlane" : qUnion([Q0])});
            skLineSegment(sketch, "E73.bottom", {"start": v(29.63, 29.64) * mm, "end": v(21.17, 29.64) * mm});
            skLineSegment(sketch, "E73.top", {"start": v(29.63, 21.18) * mm, "end": v(21.17, 21.18) * mm});
            skLineSegment(sketch, "E73.left", {"start": v(29.63, 29.64) * mm, "end": v(29.63, 21.18) * mm});
            skLineSegment(sketch, "E73.right", {"start": v(21.17, 29.64) * mm, "end": v(21.17, 21.18) * mm});
            skLineSegment(sketch, "E74.bottom", {"start": v(-21.23, 29.64) * mm, "end": v(-29.68, 29.64) * mm});
            skLineSegment(sketch, "E74.top", {"start": v(-21.23, 21.18) * mm, "end": v(-29.68, 21.18) * mm});
            skLineSegment(sketch, "E74.left", {"start": v(-21.23, 29.64) * mm, "end": v(-21.23, 21.18) * mm});
            skLineSegment(sketch, "E74.right", {"start": v(-29.68, 29.64) * mm, "end": v(-29.68, 21.18) * mm});
            skLineSegment(sketch, "E75.bottom", {"start": v(-21.23, -21.17) * mm, "end": v(-29.68, -21.17) * mm});
            skLineSegment(sketch, "E75.top", {"start": v(-21.23, -29.63) * mm, "end": v(-29.68, -29.63) * mm});
            skLineSegment(sketch, "E75.left", {"start": v(-21.23, -21.17) * mm, "end": v(-21.23, -29.63) * mm});
            skLineSegment(sketch, "E75.right", {"start": v(-29.68, -21.17) * mm, "end": v(-29.68, -29.63) * mm});
            skLineSegment(sketch, "E76.bottom", {"start": v(29.62, -20.86) * mm, "end": v(21.17, -20.86) * mm});
            skLineSegment(sketch, "E76.top", {"start": v(29.62, -29.32) * mm, "end": v(21.17, -29.32) * mm});
            skLineSegment(sketch, "E76.left", {"start": v(29.62, -20.86) * mm, "end": v(29.62, -29.32) * mm});
            skLineSegment(sketch, "E76.right", {"start": v(21.17, -20.86) * mm, "end": v(21.17, -29.32) * mm});
            skSolve(sketch);
        }
        {
            var Q0;
            Q0 = qSketchRegion(id + "F32", true);
            extrude(context, id + "F33", {"entities" : qUnion([Q0]), "depth" : 8.46 * mm, "offsetDistance" : 25.4 * mm});
        }
        {
            var Q0;
            Q0=qCreatedBy(id+"F4.planeOp",FACE);
            cPlane(context, id + "F34", {"entities" : qUnion([Q0]), "cplaneType" : CPlaneType.OFFSET, "offset" : 8.46 * mm, "oppositeDirection" : true, "width" : 152.4 * mm, "height" : 152.4 * mm});
        }
        {
            var Q0;
            Q0=qCreatedBy(id+"F34.planeOp",FACE);
            var sketch = newSketch(context, id + "F35", { "sketchPlane" : qUnion([Q0])});
            skLineSegment(sketch, "E77.bottom", {"start": v(-21.2, 29.64) * mm, "end": v(-29.66, 29.64) * mm});
            skLineSegment(sketch, "E77.top", {"start": v(-21.2, 21.19) * mm, "end": v(-29.66, 21.19) * mm});
            skLineSegment(sketch, "E77.left", {"start": v(-21.2, 29.64) * mm, "end": v(-21.2, 21.19) * mm});
            skLineSegment(sketch, "E77.right", {"start": v(-29.66, 29.64) * mm, "end": v(-29.66, 21.19) * mm});
            skLineSegment(sketch, "E78.bottom", {"start": v(29.65, 29.65) * mm, "end": v(21.2, 29.65) * mm});
            skLineSegment(sketch, "E78.top", {"start": v(29.65, 21.2) * mm, "end": v(21.2, 21.2) * mm});
            skLineSegment(sketch, "E78.left", {"start": v(29.65, 29.65) * mm, "end": v(29.65, 21.2) * mm});
            skLineSegment(sketch, "E78.right", {"start": v(21.2, 29.65) * mm, "end": v(21.2, 21.2) * mm});
            skLineSegment(sketch, "E79.bottom", {"start": v(-21.2, -20.87) * mm, "end": v(-29.66, -20.87) * mm});
            skLineSegment(sketch, "E79.top", {"start": v(-21.2, -29.33) * mm, "end": v(-29.66, -29.33) * mm});
            skLineSegment(sketch, "E79.left", {"start": v(-21.2, -20.87) * mm, "end": v(-21.2, -29.33) * mm});
            skLineSegment(sketch, "E79.right", {"start": v(-29.66, -20.87) * mm, "end": v(-29.66, -29.33) * mm});
            skLineSegment(sketch, "E80.bottom", {"start": v(29.64, -21.16) * mm, "end": v(21.18, -21.16) * mm});
            skLineSegment(sketch, "E80.top", {"start": v(29.64, -29.62) * mm, "end": v(21.18, -29.62) * mm});
            skLineSegment(sketch, "E80.left", {"start": v(29.64, -21.16) * mm, "end": v(29.64, -29.62) * mm});
            skLineSegment(sketch, "E80.right", {"start": v(21.18, -21.16) * mm, "end": v(21.18, -29.62) * mm});
            skSolve(sketch);
        }
        {
            var Q0;
            Q0 = qSketchRegion(id + "F35", true);
            extrude(context, id + "F36", {"entities" : qUnion([Q0]), "oppositeDirection" : true, "depth" : 8.46 * mm, "offsetDistance" : 25.4 * mm});
        }
        {
            var Q0;
            Q0=qCreatedBy(id+"F25.planeOp",FACE);
            cPlane(context, id + "F37", {"entities" : qUnion([Q0]), "cplaneType" : CPlaneType.OFFSET, "offset" : 8.46 * mm, "oppositeDirection" : true, "width" : 152.4 * mm, "height" : 152.4 * mm});
        }
        {
            var Q0;
            Q0=qCreatedBy(id+"F37.planeOp",FACE);
            var sketch = newSketch(context, id + "F38", { "sketchPlane" : qUnion([Q0])});
            skLineSegment(sketch, "E81.bottom", {"start": v(-42.31, 4.15) * mm, "end": v(-33.86, 4.15) * mm});
            skLineSegment(sketch, "E81.top", {"start": v(-42.31, -4.3) * mm, "end": v(-33.86, -4.3) * mm});
            skLineSegment(sketch, "E81.left", {"start": v(-42.31, 4.15) * mm, "end": v(-42.31, -4.3) * mm});
            skLineSegment(sketch, "E81.right", {"start": v(-33.86, 4.15) * mm, "end": v(-33.86, -4.3) * mm});
            skSolve(sketch);
        }
        {
            var Q0;
            Q0 = qSketchRegion(id + "F38", true);
            extrude(context, id + "F39", {"entities" : qUnion([Q0]), "operationType" : NewBodyOperationType.ADD, "oppositeDirection" : true, "depth" : 8.46 * mm, "offsetDistance" : 25.4 * mm});
        }
    });
